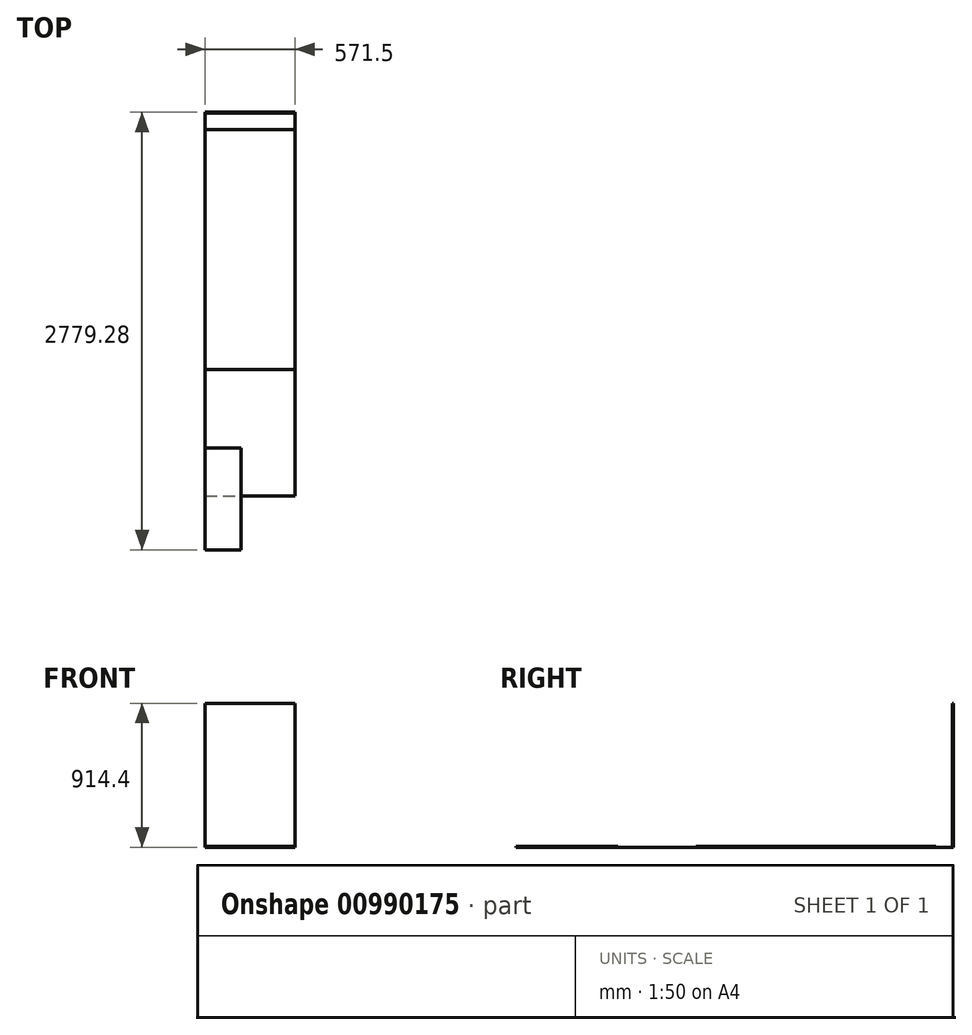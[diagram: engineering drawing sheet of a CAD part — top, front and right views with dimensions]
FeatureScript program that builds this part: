
annotation { "Feature Type Name" : "Feature", "Feature Type Description" : "" }
export const myFeature = defineFeature(function(context is Context, id is Id, definition is map)
    precondition{}
    {
        {
            var Q0;
            Q0=qCreatedBy(makeId("Top.planeOp"),FACE);
            var sketch = newSketch(context, id + "F0", { "sketchPlane" : qUnion([Q0])});
            skLineSegment(sketch, "E0.bottom", {"start": v(0, 0) * mm, "end": v(571.5, 0) * mm});
            skLineSegment(sketch, "E0.top", {"start": v(0, -2438.4) * mm, "end": v(571.5, -2438.4) * mm});
            skLineSegment(sketch, "E0.left", {"start": v(0, 0) * mm, "end": v(0, -2438.4) * mm});
            skLineSegment(sketch, "E0.right", {"start": v(571.5, 0) * mm, "end": v(571.5, -2438.4) * mm});
            skSolve(sketch);
        }
        {
            var Q0;
            Q0 = qSketchRegion(id + "F0", true);
            extrude(context, id + "F1", {"entities" : qUnion([Q0]), "depth" : 1 / 101.6 * mm, "offsetDistance" : 25.4 * mm});
        }
        {
            var Q0;
            Q0=qCreatedBy(makeId("Top.planeOp"),FACE);
            var sketch = newSketch(context, id + "F2", { "sketchPlane" : qUnion([Q0])});
            skLineSegment(sketch, "E1.bottom", {"start": v(0, 0) * mm, "end": v(571.5, 0) * mm});
            skLineSegment(sketch, "E1.top", {"start": v(0, -6.35) * mm, "end": v(571.5, -6.35) * mm});
            skLineSegment(sketch, "E1.left", {"start": v(0, 0) * mm, "end": v(0, -6.35) * mm});
            skLineSegment(sketch, "E1.right", {"start": v(571.5, 0) * mm, "end": v(571.5, -6.35) * mm});
            skSolve(sketch);
        }
        {
            var Q0;
            Q0 = qSketchRegion(id + "F2", true);
            extrude(context, id + "F3", {"entities" : qUnion([Q0]), "depth" : 914.4 * mm, "offsetDistance" : 25.4 * mm});
        }
        {
            var Q0;
            Q0=makeQuery(id+"F1.opExtrude","CAP_FACE",FACE,{"disambiguationData":[OSD([sQuery(id+"F0.wireOp",EDGE,"E0.bottom"),sQuery(id+"F0.wireOp",EDGE,"E0.top"),sQuery(id+"F0.wireOp",EDGE,"E0.left"),sQuery(id+"F0.wireOp",EDGE,"E0.right")])],"isStart":false});
            var sketch = newSketch(context, id + "F4", { "sketchPlane" : qUnion([Q0])});
            skLineSegment(sketch, "E2.bottom", {"start": v(0, -2131.58) * mm, "end": v(228.6, -2131.58) * mm});
            skLineSegment(sketch, "E2.top", {"start": v(0, -2779.28) * mm, "end": v(228.6, -2779.28) * mm});
            skLineSegment(sketch, "E2.left", {"start": v(0, -2131.58) * mm, "end": v(0, -2779.28) * mm});
            skLineSegment(sketch, "E2.right", {"start": v(228.6, -2131.58) * mm, "end": v(228.6, -2779.28) * mm});
            skSolve(sketch);
        }
        {
            var Q0;
            Q0 = qSketchRegion(id + "F4", true);
            extrude(context, id + "F5", {"entities" : qUnion([Q0]), "depth" : 6.35 * mm, "offsetDistance" : 25.4 * mm});
        }
        {
            var Q0;
            Q0=makeQuery(id+"F1.opExtrude","CAP_FACE",FACE,{"disambiguationData":[OSD([sQuery(id+"F0.wireOp",EDGE,"E0.bottom"),sQuery(id+"F0.wireOp",EDGE,"E0.top"),sQuery(id+"F0.wireOp",EDGE,"E0.left"),sQuery(id+"F0.wireOp",EDGE,"E0.right")])],"isStart":false});
            var sketch = newSketch(context, id + "F6", { "sketchPlane" : qUnion([Q0])});
            skLineSegment(sketch, "E3.bottom", {"start": v(571.5, -111.36) * mm, "end": v(0, -111.36) * mm});
            skLineSegment(sketch, "E3.top", {"start": v(571.5, -1635.36) * mm, "end": v(0, -1635.36) * mm});
            skLineSegment(sketch, "E3.left", {"start": v(571.5, -111.36) * mm, "end": v(571.5, -1635.36) * mm});
            skLineSegment(sketch, "E3.right", {"start": v(0, -111.36) * mm, "end": v(0, -1635.36) * mm});
            skSolve(sketch);
        }
        {
            var Q0;
            Q0 = qSketchRegion(id + "F6", true);
            extrude(context, id + "F7", {"entities" : qUnion([Q0]), "depth" : 6.35 * mm, "offsetDistance" : 25.4 * mm});
        }
    });
